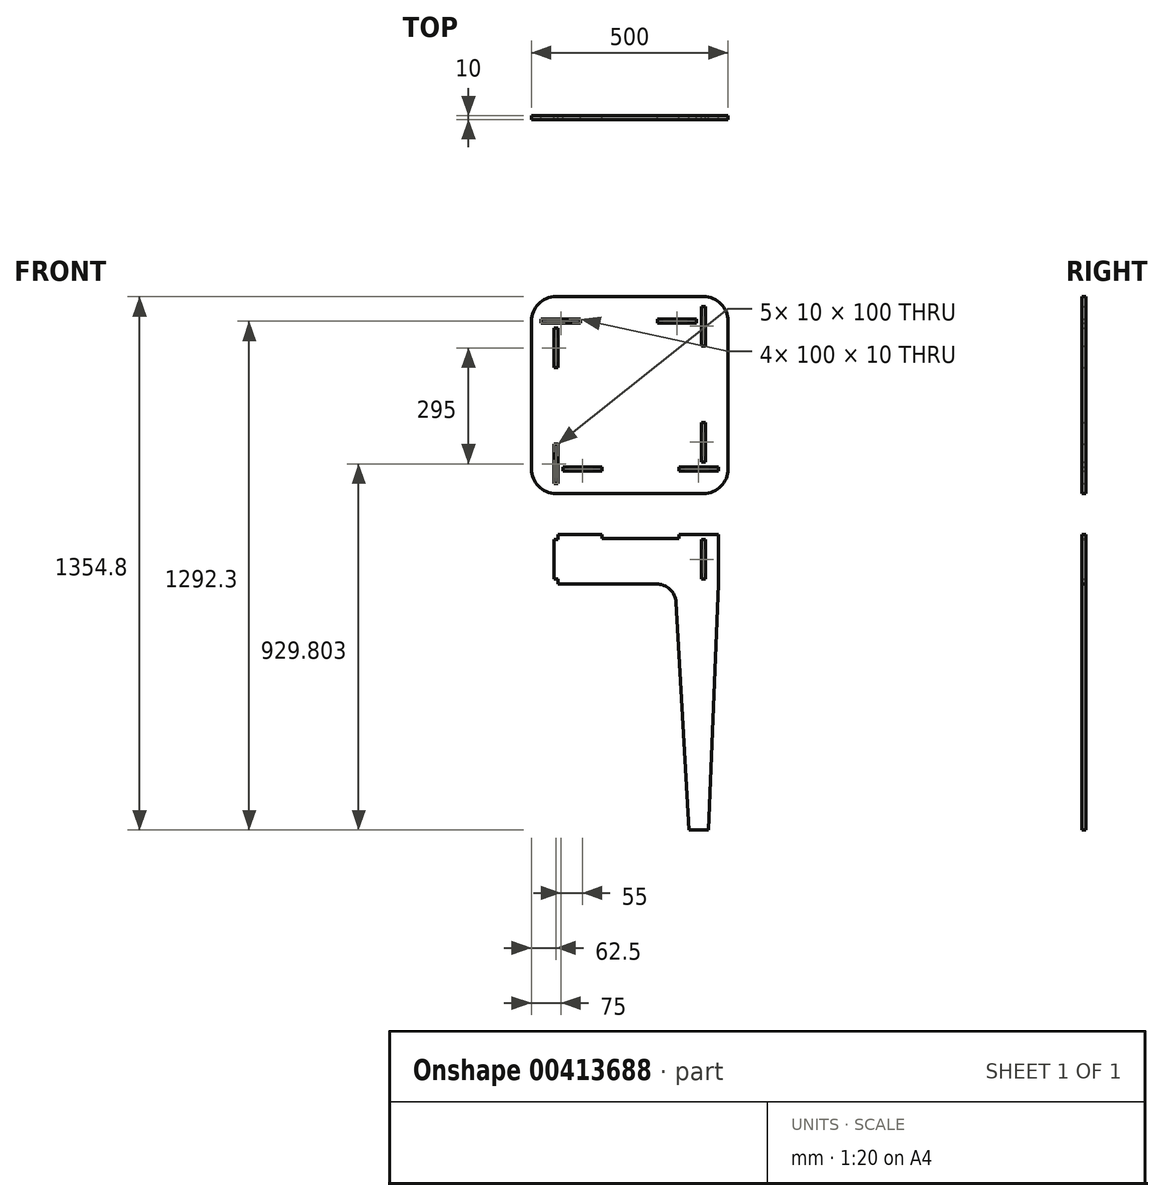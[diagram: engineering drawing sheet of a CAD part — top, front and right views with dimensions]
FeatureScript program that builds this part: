
annotation { "Feature Type Name" : "Feature", "Feature Type Description" : "" }
export const myFeature = defineFeature(function(context is Context, id is Id, definition is map)
    precondition{}
    {
        {
            var Q0;
            Q0=qCreatedBy(makeId("Front.planeOp"),FACE);
            var sketch = newSketch(context, id + "F0", { "sketchPlane" : qUnion([Q0])});
            skLineSegment(sketch, "E0", {"start": v(-187.5, 677.4) * mm, "end": v(187.5, 677.4) * mm});
            skLineSegment(sketch, "E1", {"start": v(250, 614.9) * mm, "end": v(250, 239.9) * mm});
            skLineSegment(sketch, "E2", {"start": v(187.5, 177.4) * mm, "end": v(-187.5, 177.4) * mm});
            skLineSegment(sketch, "E3", {"start": v(-250, 239.9) * mm, "end": v(-250, 614.9) * mm});
            skLineSegment(sketch, "E4", {"start": v(-225, 619.9) * mm, "end": v(-225, 609.9) * mm});
            skLineSegment(sketch, "E5", {"start": v(-225, 609.9) * mm, "end": v(-125, 609.9) * mm});
            skLineSegment(sketch, "E6", {"start": v(-125, 609.9) * mm, "end": v(-125, 619.9) * mm});
            skLineSegment(sketch, "E7", {"start": v(-125, 619.9) * mm, "end": v(-225, 619.9) * mm});
            skLineSegment(sketch, "E8", {"start": v(182.5, 552.4) * mm, "end": v(192.5, 552.4) * mm});
            skLineSegment(sketch, "E9", {"start": v(192.5, 552.4) * mm, "end": v(192.5, 652.4) * mm});
            skLineSegment(sketch, "E10", {"start": v(192.5, 652.4) * mm, "end": v(182.5, 652.4) * mm});
            skLineSegment(sketch, "E11", {"start": v(182.5, 652.4) * mm, "end": v(182.5, 552.4) * mm});
            skLineSegment(sketch, "E12", {"start": v(70, 619.9) * mm, "end": v(70, 609.9) * mm});
            skLineSegment(sketch, "E13", {"start": v(70, 609.9) * mm, "end": v(170, 609.9) * mm});
            skLineSegment(sketch, "E14", {"start": v(170, 609.9) * mm, "end": v(170, 619.9) * mm});
            skLineSegment(sketch, "E15", {"start": v(170, 619.9) * mm, "end": v(70, 619.9) * mm});
            skLineSegment(sketch, "E16", {"start": v(182.5, 257.4) * mm, "end": v(192.5, 257.4) * mm});
            skLineSegment(sketch, "E17", {"start": v(192.5, 257.4) * mm, "end": v(192.5, 357.4) * mm});
            skLineSegment(sketch, "E18", {"start": v(192.5, 357.4) * mm, "end": v(182.5, 357.4) * mm});
            skLineSegment(sketch, "E19", {"start": v(182.5, 357.4) * mm, "end": v(182.5, 257.4) * mm});
            skLineSegment(sketch, "E20", {"start": v(-182.5, 597.4) * mm, "end": v(-192.5, 597.4) * mm});
            skLineSegment(sketch, "E21", {"start": v(-192.5, 597.4) * mm, "end": v(-192.5, 497.4) * mm});
            skLineSegment(sketch, "E22", {"start": v(-192.5, 497.4) * mm, "end": v(-182.5, 497.4) * mm});
            skLineSegment(sketch, "E23", {"start": v(-182.5, 497.4) * mm, "end": v(-182.5, 597.4) * mm});
            skLineSegment(sketch, "E24", {"start": v(-182.5, 302.4) * mm, "end": v(-192.5, 302.4) * mm});
            skLineSegment(sketch, "E25", {"start": v(-192.5, 302.4) * mm, "end": v(-192.5, 202.4) * mm});
            skLineSegment(sketch, "E26", {"start": v(-182.5, 202.4) * mm, "end": v(-182.5, 302.4) * mm});
            skLineSegment(sketch, "E27", {"start": v(-192.5, 202.4) * mm, "end": v(-182.5, 202.4) * mm});
            skLineSegment(sketch, "E28", {"start": v(225, 234.9) * mm, "end": v(225, 244.9) * mm});
            skLineSegment(sketch, "E29", {"start": v(225, 244.9) * mm, "end": v(125, 244.9) * mm});
            skLineSegment(sketch, "E30", {"start": v(125, 244.9) * mm, "end": v(125, 234.9) * mm});
            skLineSegment(sketch, "E31", {"start": v(125, 234.9) * mm, "end": v(225, 234.9) * mm});
            skLineSegment(sketch, "E32", {"start": v(-70, 234.9) * mm, "end": v(-70, 244.9) * mm});
            skLineSegment(sketch, "E33", {"start": v(-70, 244.9) * mm, "end": v(-170, 244.9) * mm});
            skLineSegment(sketch, "E34", {"start": v(-170, 244.9) * mm, "end": v(-170, 234.9) * mm});
            skLineSegment(sketch, "E35", {"start": v(-170, 234.9) * mm, "end": v(-70, 234.9) * mm});
            skArc(sketch, "E36", {"start": v(-250, 239.9) * mm, "mid": v(-231.7, 195.7) * mm, "end": v(-187.5, 177.4) * mm});
            skArc(sketch, "E37", {"start": v(-187.5, 677.4) * mm, "mid": v(-231.7, 659.1) * mm, "end": v(-250, 614.9) * mm});
            skArc(sketch, "E38", {"start": v(250, 614.9) * mm, "mid": v(231.7, 659.1) * mm, "end": v(187.5, 677.4) * mm});
            skArc(sketch, "E39", {"start": v(187.5, 177.4) * mm, "mid": v(231.7, 195.7) * mm, "end": v(250, 239.9) * mm});
            skLineSegment(sketch, "E40", {"start": v(125, 62.6) * mm, "end": v(-70, 62.6) * mm});
            skLineSegment(sketch, "E41", {"start": v(-70, 72.6) * mm, "end": v(-182.5, 72.6) * mm});
            skLineSegment(sketch, "E42", {"start": v(225, 72.6) * mm, "end": v(125, 72.6) * mm});
            skLineSegment(sketch, "E43", {"start": v(125, 72.6) * mm, "end": v(125, 62.6) * mm});
            skLineSegment(sketch, "E44", {"start": v(-182.5, 72.6) * mm, "end": v(-182.5, 60.1) * mm});
            skLineSegment(sketch, "E45", {"start": v(225, 72.6) * mm, "end": v(225, -52.4) * mm});
            skLineSegment(sketch, "E46", {"start": v(67.5, -52.4) * mm, "end": v(-182.5, -52.4) * mm});
            skLineSegment(sketch, "E47", {"start": v(-70, 72.6) * mm, "end": v(-70, 62.6) * mm});
            skLineSegment(sketch, "E48", {"start": v(-192.5, -39.9) * mm, "end": v(-182.5, -39.9) * mm});
            skLineSegment(sketch, "E49", {"start": v(-182.5, 60.1) * mm, "end": v(-192.5, 60.1) * mm});
            skLineSegment(sketch, "E50", {"start": v(-192.5, 60.1) * mm, "end": v(-192.5, -39.9) * mm});
            skLineSegment(sketch, "E51", {"start": v(-182.5, -39.9) * mm, "end": v(-182.5, -52.4) * mm});
            skLineSegment(sketch, "E52", {"start": v(192.5, 60.1) * mm, "end": v(182.5, 60.1) * mm});
            skLineSegment(sketch, "E53", {"start": v(182.5, 60.1) * mm, "end": v(182.5, -39.9) * mm});
            skLineSegment(sketch, "E54", {"start": v(192.5, -39.9) * mm, "end": v(192.5, 60.1) * mm});
            skLineSegment(sketch, "E55", {"start": v(182.5, -39.9) * mm, "end": v(192.5, -39.9) * mm});
            skLineSegment(sketch, "E56", {"start": v(225, -52.4) * mm, "end": v(200, -677.4) * mm});
            skLineSegment(sketch, "E57", {"start": v(200, -677.4) * mm, "end": v(150, -677.4) * mm});
            skLineSegment(sketch, "E58", {"start": v(150, -677.4) * mm, "end": v(117.42, -99.59) * mm});
            skPoint(sketch, "E59.visualSharp", {"position": v(114.76, -52.4) * mm});
            skArc(sketch, "E59.filletArc", {"start": v(117.42, -99.59) * mm, "mid": v(101.85, -66.07) * mm, "end": v(67.5, -52.4) * mm});
            skLineSegment(sketch, "E60", {"start": v(-250, 427.4) * mm, "end": v(250, 427.4) * mm});
            skLineSegment(sketch, "E61", {"start": v(0, 677.4) * mm, "end": v(0, 177.4) * mm});
            skSolve(sketch);
        }
        {
            var Q0;
            Q0 = qSketchRegion(id + "F0", true);
            extrude(context, id + "F1", {"entities" : qUnion([Q0]), "depth" : 10 * mm});
        }
    });
